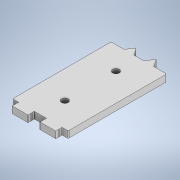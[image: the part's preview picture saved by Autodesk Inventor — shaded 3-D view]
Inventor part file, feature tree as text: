
AUTODESK INVENTOR PART (.ipt)
format: ipt  version: 2020 (Build 240168000, 168)  size: 145,408 bytes
history: native  units: mm
features: extrude x1, sketch x1
ambient origin geometry x8: Origin, YZ Plane, XZ Plane, XY Plane, X Axis, Y Axis, Z Axis, Center Point
bodies: Solid1 (feature_tree)
feature tree (2):
  extrude  "Extrusion1"  [1 undecoded]
  sketch  "Sketch1"  dims[d0=3.0mm d1=0.0mm]
note: 1 required parameter value undecoded (feature->parameter linkage not recoverable at this tier; creation-order binding heuristic only, values carry confidence <= 0.55)
